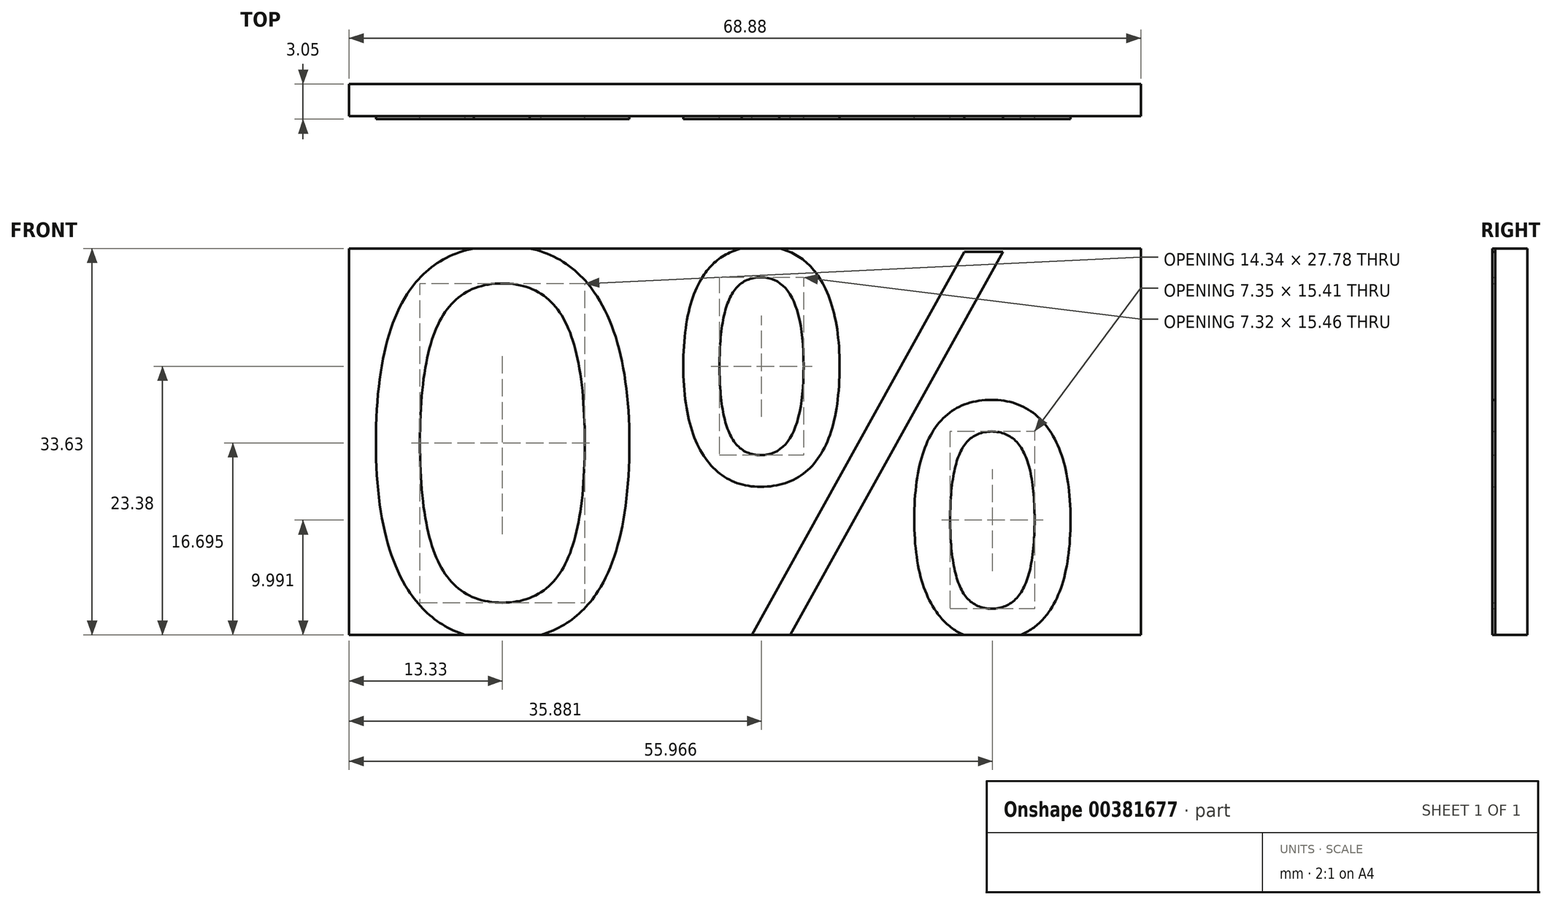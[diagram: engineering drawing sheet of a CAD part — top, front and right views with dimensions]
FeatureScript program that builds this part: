
annotation { "Feature Type Name" : "Feature", "Feature Type Description" : "" }
export const myFeature = defineFeature(function(context is Context, id is Id, definition is map)
    precondition{}
    {
        {
            var Q0;
            Q0=qCreatedBy(makeId("Front.planeOp"),FACE);
            var sketch = newSketch(context, id + "F0", { "sketchPlane" : qUnion([Q0])});
            skLineSegment(sketch, "E0.bottom", {"start": v(-34.44, 33.63) * mm, "end": v(34.44, 33.63) * mm});
            skLineSegment(sketch, "E0.top", {"start": v(-34.44, 0) * mm, "end": v(34.44, 0) * mm});
            skLineSegment(sketch, "E0.left", {"start": v(-34.44, 33.63) * mm, "end": v(-34.44, 0) * mm});
            skLineSegment(sketch, "E0.right", {"start": v(34.44, 33.63) * mm, "end": v(34.44, 0) * mm});
            skSolve(sketch);
        }
        {
            var Q0;
            Q0 = qSketchRegion(id + "F0", true);
            extrude(context, id + "F1", {"entities" : qUnion([Q0]), "depth" : 2.8 * mm});
        }
        {
            var Q0;
            Q0=makeQuery(id+"F1.opExtrude","CAP_FACE",FACE,{"disambiguationData":[OSD([sQuery(id+"F0.wireOp",EDGE,"E0.bottom"),sQuery(id+"F0.wireOp",EDGE,"E0.top"),sQuery(id+"F0.wireOp",EDGE,"E0.left"),sQuery(id+"F0.wireOp",EDGE,"E0.right")])],"isStart":false});
            var sketch = newSketch(context, id + "F2", { "sketchPlane" : qUnion([Q0])});
            skText(sketch, "E1", { "text": "0%", "fontName": "OpenSans-Regular.ttf"});
            const initialGuessF2  = {"E1": [-0.03444, 0, 1, 0, 0.03363]};
            skSetInitialGuess(sketch, initialGuessF2);
            skSolve(sketch);
        }
        {
            var Q0;
            {var subQ7=sQuery(id+"F2.wireOp",EDGE,"E1.sketch_text.stroke-0");Q0=makeQuery(id+"F2.imprint","IMPRINT",FACE,{"disambiguationData":[TD([[makeQuery(id+"F2.imprint","IMPRINT",EDGE,{"derivedFrom":subQ7}),-1.0]])]});}
            var Q1;
            Q1=makeQuery(id+"F2.imprint","IMPRINT",FACE,{"disambiguationData":[TD([[makeQuery(id+"F2.imprint","IMPRINT",EDGE,{"derivedFrom":sQuery(id+"F2.wireOp",EDGE,"E1.sketch_text.stroke-16")}),-1.0]])]});
            var Q2;
            Q2=makeQuery(id+"F2.imprint","IMPRINT",FACE,{"disambiguationData":[TD([[makeQuery(id+"F2.imprint","IMPRINT",EDGE,{"derivedFrom":sQuery(id+"F2.wireOp",EDGE,"E1.sketch_text.stroke-30")}),-1.0]])]});
            var Q3;
            Q3=makeQuery(id+"F2.imprint","IMPRINT",FACE,{"disambiguationData":[TD([[makeQuery(id+"F2.imprint","IMPRINT",EDGE,{"derivedFrom":sQuery(id+"F2.wireOp",EDGE,"E1.sketch_text.stroke-46")}),-1.0]])]});
            extrude(context, id + "F3", {"entities" : qUnion([Q0, Q1, Q2, Q3]), "depth" : 0.25 * mm});
        }
    });
